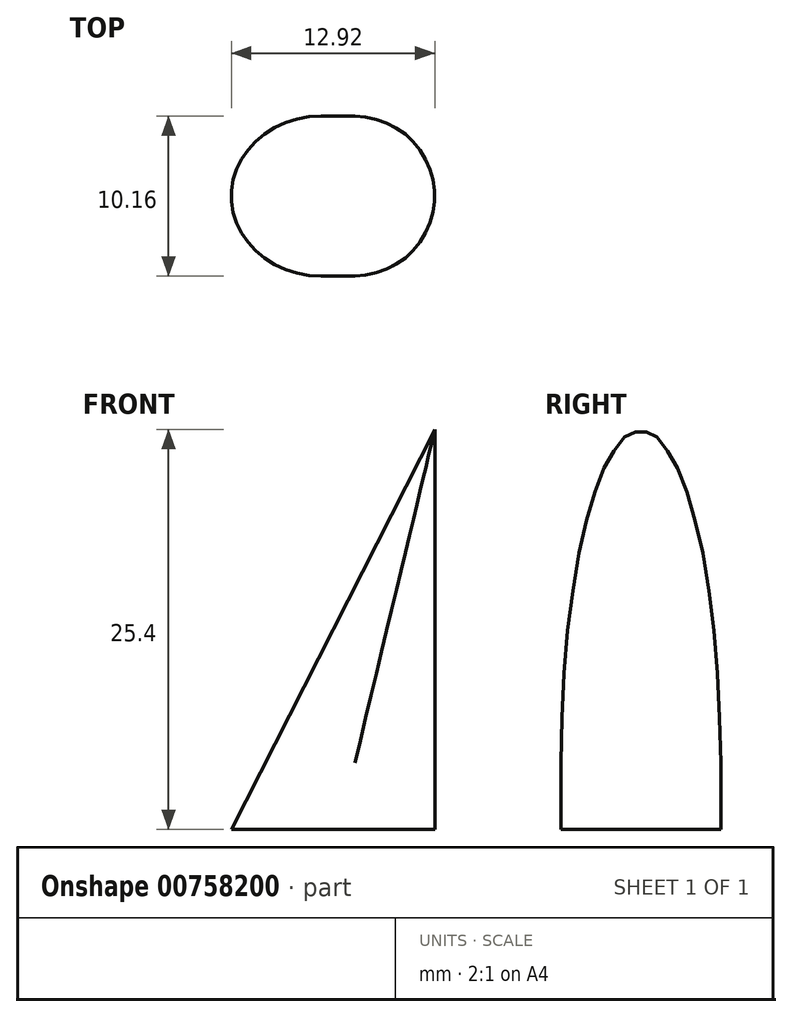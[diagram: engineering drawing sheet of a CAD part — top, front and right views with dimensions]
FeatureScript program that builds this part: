
annotation { "Feature Type Name" : "Feature", "Feature Type Description" : "" }
export const myFeature = defineFeature(function(context is Context, id is Id, definition is map)
    precondition{}
    {
        {
            var Q0;
            Q0=qCreatedBy(makeId("Front.planeOp"),FACE);
            var sketch = newSketch(context, id + "F0", { "sketchPlane" : qUnion([Q0])});
            skLineSegment(sketch, "E0", {"start": v(0, 0) * mm, "end": v(-12.92, 0) * mm});
            skLineSegment(sketch, "E1", {"start": v(-12.92, 0) * mm, "end": v(0, 25.4) * mm});
            skLineSegment(sketch, "E2", {"start": v(0, 25.4) * mm, "end": v(0, 0) * mm});
            skSolve(sketch);
        }
        {
            var Q0;
            Q0=makeQuery(id+"F0.imprint","IMPRINT",FACE,{"disambiguationData":[TD([[makeQuery(id+"F0.imprint","IMPRINT",EDGE,{"derivedFrom":sQuery(id+"F0.wireOp",EDGE,"E0")}),-1.0]])]});
            extrude(context, id + "F1", {"entities" : qUnion([Q0]), "depth" : 10.16 * mm, "offsetDistance" : 25.4 * mm});
        }
        {
            var Q0;
            Q0=makeQuery(id+"F1.opExtrude","CAP_EDGE",EDGE,{"disambiguationData":[OSD([sQuery(id+"F0.wireOp",EDGE,"E1")])],"isStart":true});
            var Q1;
            Q1=makeQuery(id+"F1.opExtrude","CAP_EDGE",EDGE,{"disambiguationData":[OSD([sQuery(id+"F0.wireOp",EDGE,"E1")])],"isStart":false});
            var Q2;
            Q2=makeQuery(id+"F1.opExtrude","CAP_EDGE",EDGE,{"disambiguationData":[OSD([sQuery(id+"F0.wireOp",EDGE,"E2")])],"isStart":true});
            var Q3;
            Q3=makeQuery(id+"F1.opExtrude","CAP_EDGE",EDGE,{"disambiguationData":[OSD([sQuery(id+"F0.wireOp",EDGE,"E2")])],"isStart":false});
            fillet(context, id + "F2", {"entities" : qUnion([Q0, Q1, Q2, Q3]), "radius" : 5.08 * mm, "tangentPropagation" : true, "allowEdgeOverflow" : false});
        }
    });
